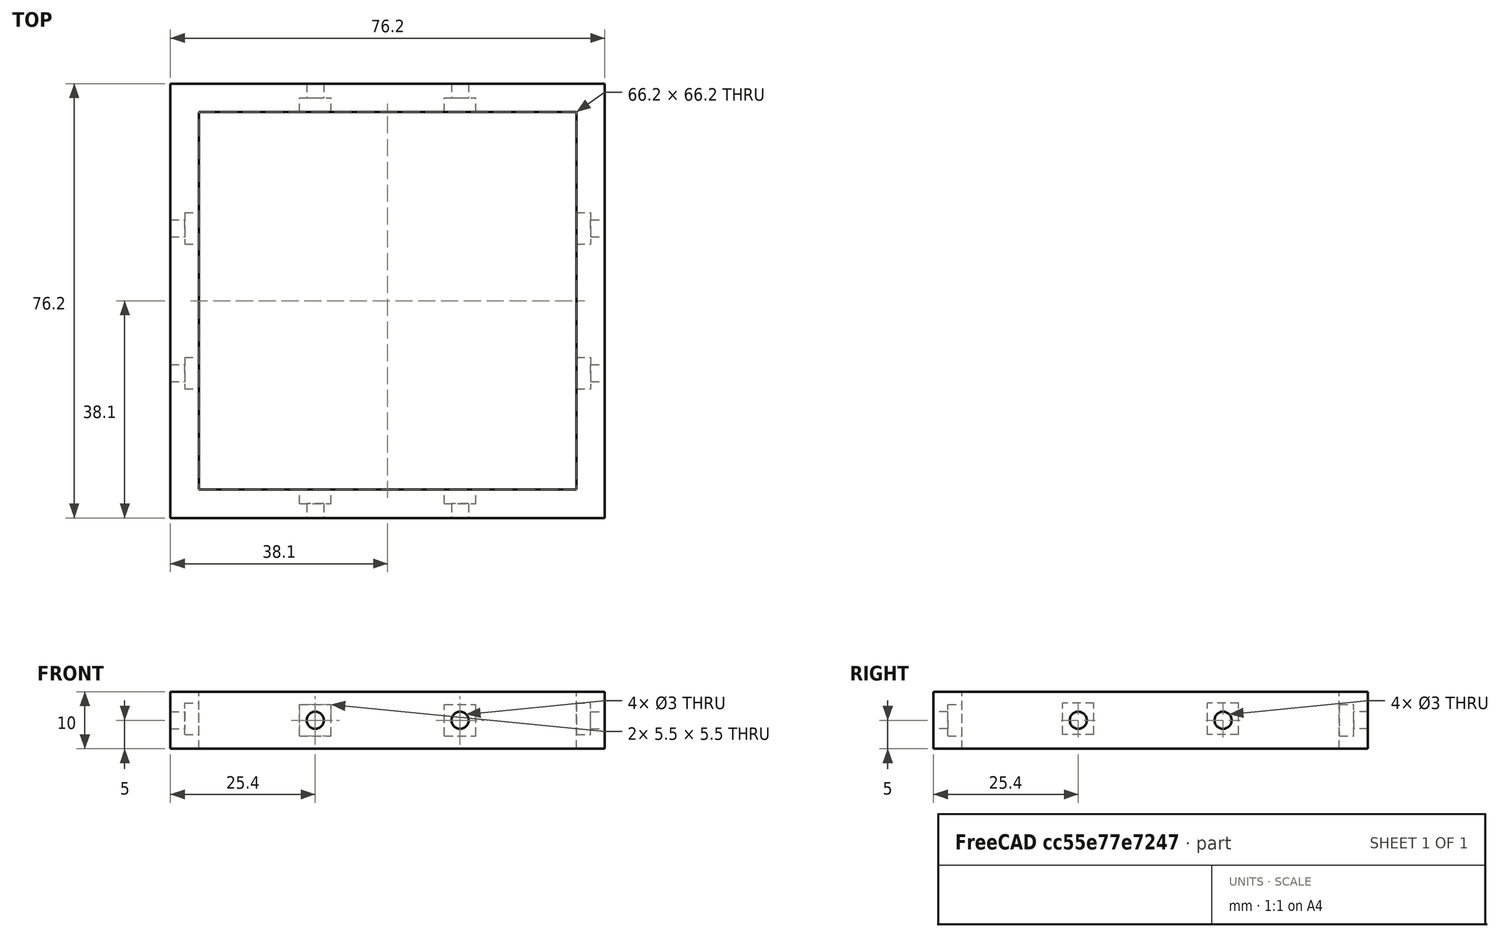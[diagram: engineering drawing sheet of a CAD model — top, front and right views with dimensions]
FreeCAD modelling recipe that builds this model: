
FCSTD DOCUMENT
Label: thinside
objects: Part::Cut×17, Part::Box×10, Part::Cylinder×8
note: 35 computed .brp shape members not serialized (recipe doc carries the construction recipe); baked Part::Feature solids carry a one-line shape summary decoded from their .brp

FEATURE [Part::Box] Box
  Height = 10
  Length = 76.2
  Width = 76.2
FEATURE [Part::Box] Box001
  Height = 10
  Length = 66.2
  Placement = pos=(5,5,0) rot=(0,0,1;0rad)
  Width = 66.2
FEATURE [Part::Cut] Cut
  Base = -> Box
  Tool = -> Box001
FEATURE [Part::Box] Box002
  Height = 5.5
  Length = 5.5
  Placement = pos=(22.65,2.5,2.25) rot=(0,0,1;0rad)
  Width = 2.5
FEATURE [Part::Box] Box003
  Height = 5.5
  Length = 5.5
  Placement = pos=(48.05,2.5,2.25) rot=(0,0,1;0rad)
  Width = 2.5
FEATURE [Part::Cut] Cut001
  Base = -> Cut
  Tool = -> Box002
FEATURE [Part::Cut] Cut002
  Base = -> Cut001
  Tool = -> Box003
FEATURE [Part::Box] Box004
  Height = 5.5
  Length = 5.5
  Placement = pos=(48.05,71.19,2.25) rot=(0,0,1;0rad)
  Width = 2.5
FEATURE [Part::Box] Box005
  Height = 5.5
  Length = 5.5
  Placement = pos=(22.65,71.19,2.25) rot=(0,0,1;0rad)
  Width = 2.5
FEATURE [Part::Cut] Cut003
  Base = -> Cut002
  Tool = -> Box004
FEATURE [Part::Cut] Cut004
  Base = -> Cut003
  Tool = -> Box005
FEATURE [Part::Box] Box006
  Height = 5.5
  Length = 5.5
  Placement = pos=(2.5,28.15,2.5) rot=(0,0,-1;1.5708rad)
  Width = 2.5
FEATURE [Part::Box] Box007
  Height = 5.5
  Length = 5.5
  Placement = pos=(2.5,53.55,2.5) rot=(0,0,-1;1.5708rad)
  Width = 2.5
FEATURE [Part::Box] Box008
  Height = 5.5
  Length = 5.5
  Placement = pos=(71.19,28.15,2.5) rot=(0,0,-1;1.5708rad)
  Width = 2.5
FEATURE [Part::Box] Box009
  Height = 5.5
  Length = 5.5
  Placement = pos=(71.19,53.55,2.5) rot=(0,0,-1;1.5708rad)
  Width = 2.5
FEATURE [Part::Cut] Cut005
  Base = -> Cut004
  Tool = -> Box006
FEATURE [Part::Cut] Cut006
  Base = -> Cut005
  Tool = -> Box007
FEATURE [Part::Cut] Cut007
  Base = -> Cut006
  Tool = -> Box009
FEATURE [Part::Cut] Cut008
  Base = -> Cut007
  Tool = -> Box008
FEATURE [Part::Cylinder] Cylinder
  Angle = 360
  Height = 5
  Placement = pos=(0,25.4,5) rot=(0,1,0;1.5708rad)
  Radius = 1.5
FEATURE [Part::Cylinder] Cylinder001
  Angle = 360
  Height = 5
  Placement = pos=(0,50.8,5) rot=(0,1,0;1.5708rad)
  Radius = 1.5
FEATURE [Part::Cylinder] Cylinder002
  Angle = 360
  Height = 5
  Placement = pos=(71.2,50.8,5) rot=(0,1,0;1.5708rad)
  Radius = 1.5
FEATURE [Part::Cylinder] Cylinder003
  Angle = 360
  Height = 5
  Placement = pos=(71.2,25.4,5) rot=(0,1,0;1.5708rad)
  Radius = 1.5
FEATURE [Part::Cylinder] Cylinder004
  Angle = 360
  Height = 5
  Placement = pos=(25.4,5,5) rot=(1,0,0;1.5708rad)
  Radius = 1.5
FEATURE [Part::Cylinder] Cylinder005
  Angle = 360
  Height = 5
  Placement = pos=(50.8,5,5) rot=(1,0,0;1.5708rad)
  Radius = 1.5
FEATURE [Part::Cylinder] Cylinder006
  Angle = 360
  Height = 5
  Placement = pos=(50.8,76.2,5) rot=(1,0,0;1.5708rad)
  Radius = 1.5
FEATURE [Part::Cylinder] Cylinder007
  Angle = 360
  Height = 5
  Placement = pos=(25.4,76.2,5) rot=(1,0,0;1.5708rad)
  Radius = 1.5
FEATURE [Part::Cut] Cut009
  Base = -> Cut008
  Tool = -> Cylinder
FEATURE [Part::Cut] Cut010
  Base = -> Cut009
  Tool = -> Cylinder007
FEATURE [Part::Cut] Cut011
  Base = -> Cut010
  Tool = -> Cylinder006
FEATURE [Part::Cut] Cut012
  Base = -> Cut011
  Tool = -> Cylinder005
FEATURE [Part::Cut] Cut013
  Base = -> Cut012
  Tool = -> Cylinder004
FEATURE [Part::Cut] Cut014
  Base = -> Cut013
  Tool = -> Cylinder003
FEATURE [Part::Cut] Cut015
  Base = -> Cut014
  Tool = -> Cylinder002
FEATURE [Part::Cut] Cut016
  Base = -> Cut015
  Tool = -> Cylinder001
